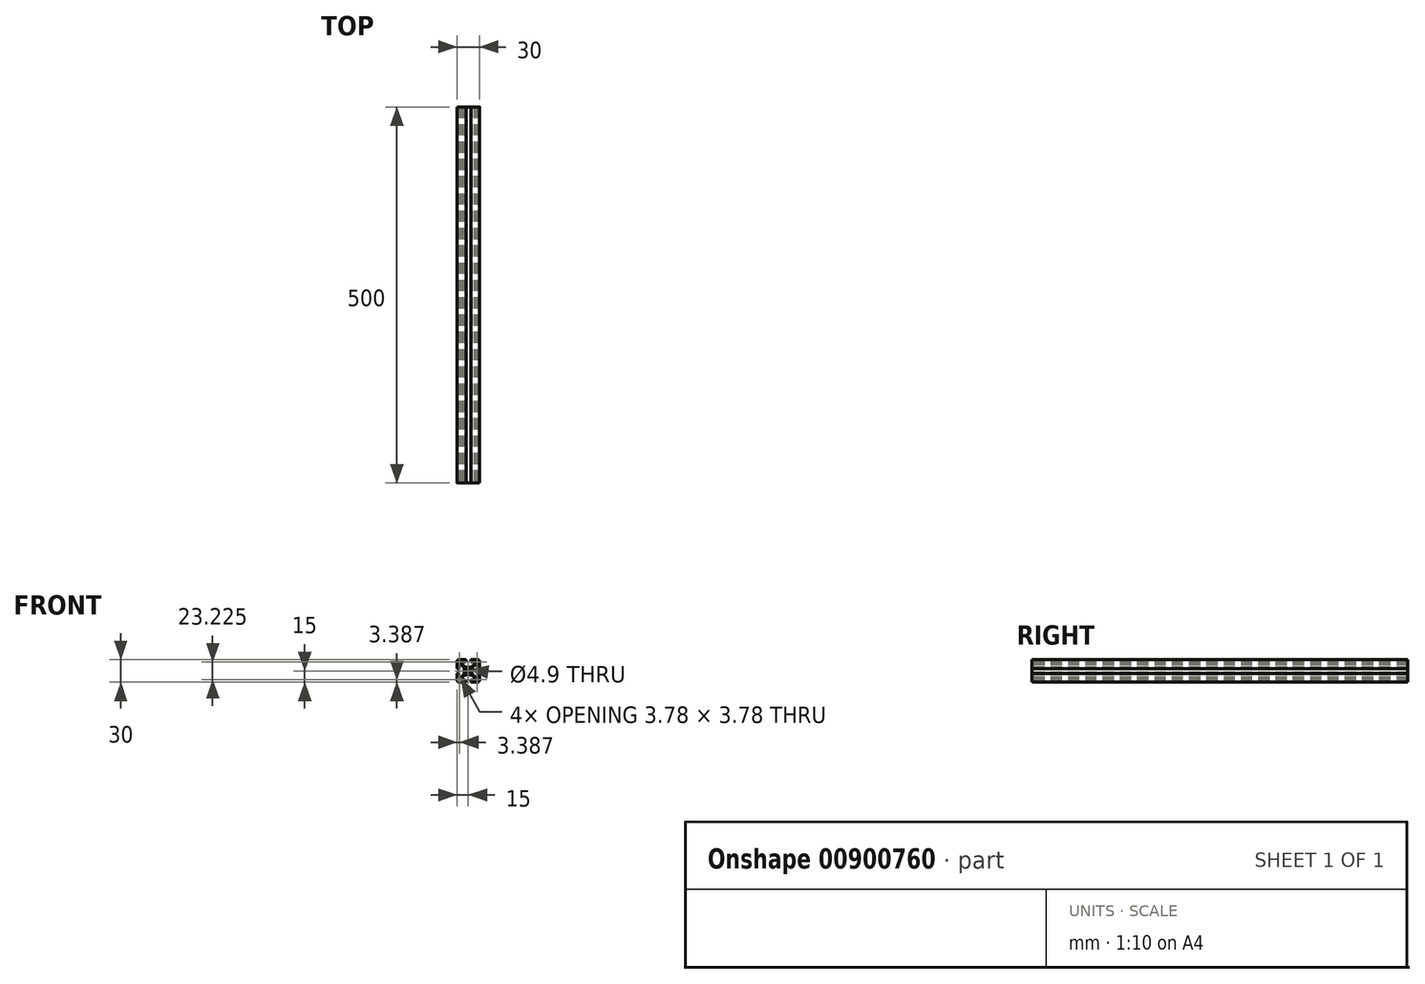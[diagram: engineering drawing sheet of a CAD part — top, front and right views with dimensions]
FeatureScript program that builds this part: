
annotation { "Feature Type Name" : "Feature", "Feature Type Description" : "" }
export const myFeature = defineFeature(function(context is Context, id is Id, definition is map)
    precondition{}
    {
        {
            var Q0;
            Q0=qCreatedBy(makeId("Front.planeOp"),FACE);
            var sketch = newSketch(context, id + "F0", { "sketchPlane" : qUnion([Q0])});
            skLineSegment(sketch, "E0", {"start": v(0, 28.3) * mm, "end": v(0, 2.45) * mm, "construction": true});
            skLineSegment(sketch, "E1", {"start": v(0, 0) * mm, "end": v(55.3, 55.3) * mm, "construction": true});
            skLineSegment(sketch, "E2", {"start": v(0, 5.1) * mm, "end": v(4.04, 5.1) * mm});
            skLineSegment(sketch, "E3", {"start": v(4.04, 5.1) * mm, "end": v(8.22, 9.29) * mm});
            skLineSegment(sketch, "E4", {"start": v(8.22, 9.29) * mm, "end": v(8.22, 13.5) * mm});
            skLineSegment(sketch, "E5", {"start": v(8.22, 13.5) * mm, "end": v(5.47, 13.5) * mm});
            skLineSegment(sketch, "E6", {"start": v(5.47, 13.5) * mm, "end": v(5.47, 12.1) * mm});
            skLineSegment(sketch, "E7", {"start": v(5.47, 12.1) * mm, "end": v(3.17, 12.1) * mm});
            skLineSegment(sketch, "E8", {"start": v(3.17, 12.1) * mm, "end": v(3.17, 15) * mm});
            skLineSegment(sketch, "E9", {"start": v(3.17, 15) * mm, "end": v(15, 15) * mm});
            skArc(sketch, "E10", {"start": v(1.73, 1.73) * mm, "mid": v(0.94, 2.26) * mm, "end": v(0, 2.45) * mm});
            skLineSegment(sketch, "E11.trimOffspring", {"start": v(0, 0) * mm, "end": v(0, -28.3) * mm, "construction": true});
            skPoint(sketch, "E12.visualSharp", {"position": v(3.17, 12.1) * mm});
            skLineSegment(sketch, "E13", {"start": v(0, 5.1) * mm, "end": v(0, 2.45) * mm});
            skLineSegment(sketch, "E14", {"start": v(1.73, 1.73) * mm, "end": v(15, 15) * mm});
            skSolve(sketch);
        }
        {
            var Q0;
            {var subQ1=sQuery(id+"F0.wireOp",EDGE,"E2");Q0=makeQuery(id+"F0.imprint","IMPRINT",FACE,{"disambiguationData":[TD([[makeQuery(id+"F0.imprint","IMPRINT",EDGE,{"derivedFrom":subQ1}),-1.0]])]});}
            extrude(context, id + "F1", {"entities" : qUnion([Q0]), "oppositeDirection" : true, "depth" : 500 * mm, "offsetDistance" : 25 * mm});
        }
        {
            var Q0;
            Q0=makeQuery(id+"F1.opExtrude","SWEPT_EDGE",EDGE,{"disambiguationData":[OSD([sQuery(id+"F0.wireOp",EDGE,"E2"),sQuery(id+"F0.wireOp",EDGE,"E3")])]});
            var Q1;
            Q1=makeQuery(id+"F1.opExtrude","SWEPT_EDGE",EDGE,{"disambiguationData":[OSD([sQuery(id+"F0.wireOp",EDGE,"E3"),sQuery(id+"F0.wireOp",EDGE,"E4")])]});
            fillet(context, id + "F2", {"entities" : qUnion([Q0, Q1]), "radius" : 2 * mm, "tangentPropagation" : true, "allowEdgeOverflow" : false});
        }
        {
            var Q0;
            Q0=makeQuery(id+"F1.opExtrude","SWEPT_EDGE",EDGE,{"disambiguationData":[OSD([sQuery(id+"F0.wireOp",EDGE,"E7"),sQuery(id+"F0.wireOp",EDGE,"E8")])]});
            var Q1;
            Q1=makeQuery(id+"F1.opExtrude","SWEPT_EDGE",EDGE,{"disambiguationData":[OSD([sQuery(id+"F0.wireOp",EDGE,"E6"),sQuery(id+"F0.wireOp",EDGE,"E7")])]});
            var Q2;
            Q2=makeQuery(id+"F1.opExtrude","SWEPT_EDGE",EDGE,{"disambiguationData":[OSD([sQuery(id+"F0.wireOp",EDGE,"E8"),sQuery(id+"F0.wireOp",EDGE,"E9")])]});
            fillet(context, id + "F3", {"entities" : qUnion([Q0, Q1, Q2]), "radius" : 0.75 * mm, "tangentPropagation" : true, "allowEdgeOverflow" : false});
        }
        {
            var Q0;
            Q0=makeQuery(id+"F1.opExtrude","SWEPT_EDGE",EDGE,{"disambiguationData":[OSD([sQuery(id+"F0.wireOp",EDGE,"E5"),sQuery(id+"F0.wireOp",EDGE,"E6")])]});
            var Q1;
            Q1=makeQuery(id+"F1.opExtrude","SWEPT_EDGE",EDGE,{"disambiguationData":[OSD([sQuery(id+"F0.wireOp",EDGE,"E4"),sQuery(id+"F0.wireOp",EDGE,"E5")])]});
            fillet(context, id + "F4", {"entities" : qUnion([Q0, Q1]), "radius" : 0.75 * mm, "tangentPropagation" : true, "allowEdgeOverflow" : false});
        }
        {
            var Q0;
            Q0=makeQuery(id+"F1.opExtrude","SWEPT_BODY",BODY,{"disambiguationData":[OSD([sQuery(id+"F0.wireOp",EDGE,"E2"),sQuery(id+"F0.wireOp",EDGE,"E3"),sQuery(id+"F0.wireOp",EDGE,"E4"),sQuery(id+"F0.wireOp",EDGE,"E5"),sQuery(id+"F0.wireOp",EDGE,"E6"),sQuery(id+"F0.wireOp",EDGE,"E7"),sQuery(id+"F0.wireOp",EDGE,"E8"),sQuery(id+"F0.wireOp",EDGE,"E9"),sQuery(id+"F0.wireOp",EDGE,"E10"),sQuery(id+"F0.wireOp",EDGE,"E13"),sQuery(id+"F0.wireOp",EDGE,"E14")])]});
            var Q1;
            Q1=makeQuery(id+"F1.opExtrude","SWEPT_FACE",FACE,{"disambiguationData":[OSD([sQuery(id+"F0.wireOp",EDGE,"E14")])]});
            mirror(context, id + "F5", {"operationType" : NewBodyOperationType.ADD, "entities" : qUnion([Q0]), "mirrorPlane" : qUnion([Q1])});
        }
        {
            var Q0;
            {var subQ0=makeQuery(id+"F1.opExtrude","SWEPT_EDGE",EDGE,{"disambiguationData":[OSD([sQuery(id+"F0.wireOp",EDGE,"E9"),sQuery(id+"F0.wireOp",EDGE,"E14")])]});Q0=makeQuery(id+"F5.boolean.opBoolean","MERGE",EDGE,{"derivedFrom":[subQ0,makeQuery(id+"F5.opPattern","COPY",EDGE,{"derivedFrom":subQ0,"instanceName":"1"})]});}
            fillet(context, id + "F6", {"entities" : qUnion([Q0]), "radius" : 3 * mm, "tangentPropagation" : true, "allowEdgeOverflow" : false});
        }
        {
            var Q0;
            Q0=qCreatedBy(makeId("Front.planeOp"),FACE);
            var sketch = newSketch(context, id + "F7", { "sketchPlane" : qUnion([Q0])});
            skLineSegment(sketch, "E15", {"start": v(9.72, 13.5) * mm, "end": v(9.72, 9.72) * mm});
            skLineSegment(sketch, "E16", {"start": v(9.72, 9.72) * mm, "end": v(13.5, 9.72) * mm});
            skLineSegment(sketch, "E17", {"start": v(13.5, 9.72) * mm, "end": v(13.5, 12) * mm});
            skArc(sketch, "E18", {"start": v(13.5, 12) * mm, "mid": v(13.06, 13.06) * mm, "end": v(12, 13.5) * mm});
            skLineSegment(sketch, "E19", {"start": v(12, 13.5) * mm, "end": v(9.72, 13.5) * mm});
            skLineSegment(sketch, "E20", {"start": v(9.72, 13.5) * mm, "end": v(9.72, 15) * mm, "construction": true});
            skLineSegment(sketch, "E21", {"start": v(9.72, 11.61) * mm, "end": v(8.22, 11.61) * mm, "construction": true});
            skLineSegment(sketch, "E22", {"start": v(11.61, 9.72) * mm, "end": v(11.61, 8.22) * mm, "construction": true});
            skSolve(sketch);
        }
        {
            var Q0;
            Q0=makeQuery(id+"F7.imprint","IMPRINT",FACE,{"disambiguationData":[TD([[makeQuery(id+"F7.imprint","IMPRINT",EDGE,{"derivedFrom":sQuery(id+"F7.wireOp",EDGE,"E15")}),1.0]])]});
            extrude(context, id + "F8", {"entities" : qUnion([Q0]), "operationType" : NewBodyOperationType.REMOVE, "endBound" : BoundingType.THROUGH_ALL, "oppositeDirection" : true, "depth" : 25 * mm, "offsetDistance" : 25 * mm});
        }
        {
            var Q0;
            Q0=qCreatedBy(makeId("Right.planeOp"),FACE);
            var sketch = newSketch(context, id + "F9", { "sketchPlane" : qUnion([Q0])});
            skLineSegment(sketch, "E23", {"start": v(0, 0) * mm, "end": v(12.06, 0) * mm, "construction": true});
            skSolve(sketch);
        }
        {
            var Q0;
            Q0=makeQuery(id+"F1.opExtrude","SWEPT_BODY",BODY,{"disambiguationData":[OSD([sQuery(id+"F0.wireOp",EDGE,"E2"),sQuery(id+"F0.wireOp",EDGE,"E3"),sQuery(id+"F0.wireOp",EDGE,"E4"),sQuery(id+"F0.wireOp",EDGE,"E5"),sQuery(id+"F0.wireOp",EDGE,"E6"),sQuery(id+"F0.wireOp",EDGE,"E7"),sQuery(id+"F0.wireOp",EDGE,"E8"),sQuery(id+"F0.wireOp",EDGE,"E9"),sQuery(id+"F0.wireOp",EDGE,"E10"),sQuery(id+"F0.wireOp",EDGE,"E13"),sQuery(id+"F0.wireOp",EDGE,"E14")])]});
            var Q1;
            Q1=sQuery(id+"F9.wireOp",EDGE,"E23");
            circularPattern(context, id + "F10", {"operationType" : NewBodyOperationType.ADD, "entities" : qUnion([Q0]), "axis" : qUnion([Q1]), "angle" : 360 * degree, "instanceCount" : 4, "equalSpace" : true});
        }
    });
